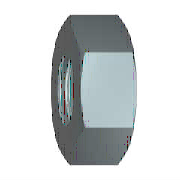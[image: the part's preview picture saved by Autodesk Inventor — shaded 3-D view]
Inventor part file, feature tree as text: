
AUTODESK INVENTOR PART (.ipt)
format: ipt  version: 2015 (Build 190159000, 159)  size: 164,352 bytes
history: native  units: mm (DEFAULTED — no unit token found)
features: sketch x3, other x2, extrude x1, hole x1, plane x1
ambient origin geometry x7: Origin, YZ Plane, XZ Plane, X Axis, Y Axis, Z Axis, Center Point
bodies: Body1 (feature_tree)
feature tree (8):
  extrude  "Bryła"  Depth=15.011107mm
  other  "Faza1"
  hole  "Gwint"  [1 undecoded]
  other  "Work Axis1"
  plane  "Work Plane1"
  sketch  "Szkic1"
  sketch  "Szkic2"
  sketch  "Szkic3"
note: 1 required parameter value undecoded (feature->parameter linkage not recoverable at this tier; creation-order binding heuristic only, values carry confidence <= 0.55)
